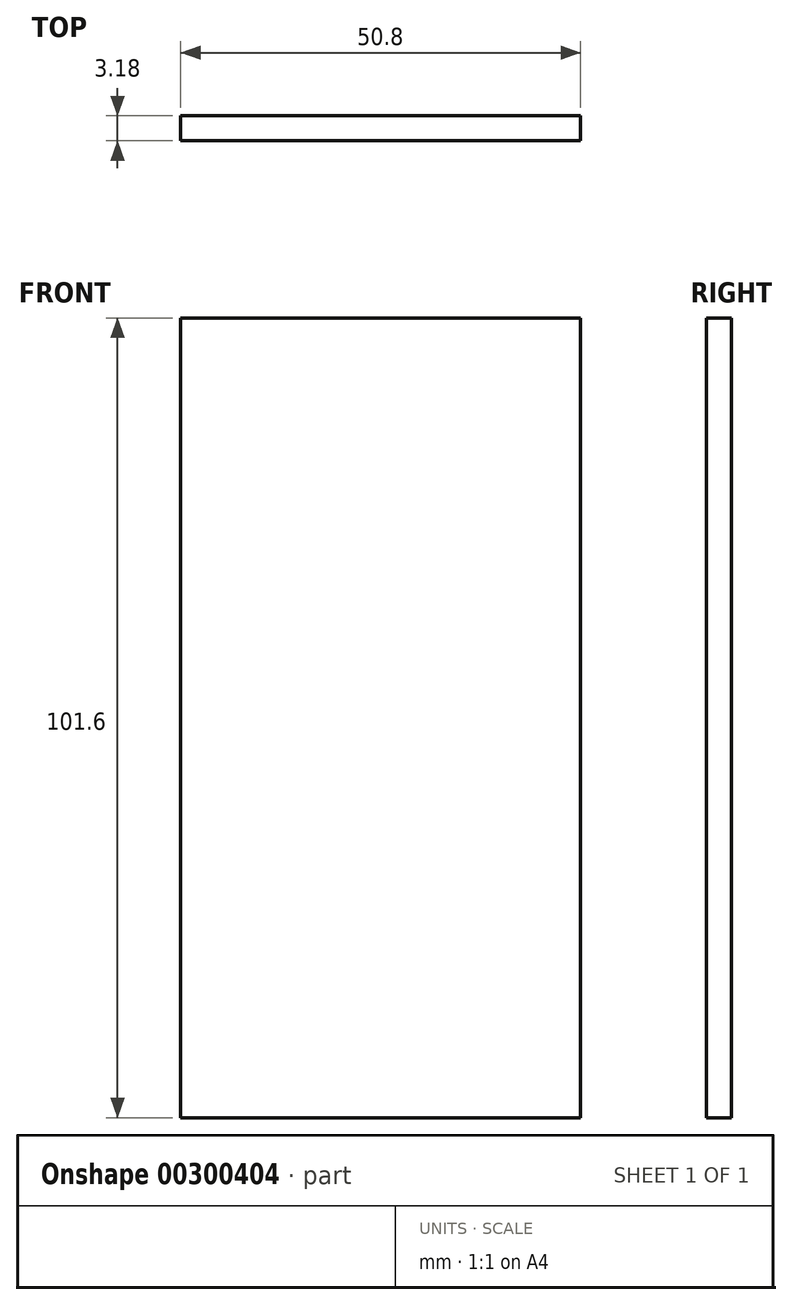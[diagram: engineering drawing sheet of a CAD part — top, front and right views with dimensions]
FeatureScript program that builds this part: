
annotation { "Feature Type Name" : "Feature", "Feature Type Description" : "" }
export const myFeature = defineFeature(function(context is Context, id is Id, definition is map)
    precondition{}
    {
        {
            var Q0;
            Q0=qCreatedBy(makeId("Front.planeOp"),FACE);
            var sketch = newSketch(context, id + "F0", { "sketchPlane" : qUnion([Q0])});
            skLineSegment(sketch, "E0.bottom", {"start": v(25.4, 50.8) * mm, "end": v(-25.4, 50.8) * mm});
            skLineSegment(sketch, "E0.top", {"start": v(25.4, -50.8) * mm, "end": v(-25.4, -50.8) * mm});
            skLineSegment(sketch, "E0.left", {"start": v(25.4, 50.8) * mm, "end": v(25.4, -50.8) * mm});
            skLineSegment(sketch, "E0.right", {"start": v(-25.4, 50.8) * mm, "end": v(-25.4, -50.8) * mm});
            skPoint(sketch, "E0.middle", {"position": v(0, 0) * mm});
            skSolve(sketch);
        }
        {
            var Q0;
            Q0 = qSketchRegion(id + "F0", true);
            extrude(context, id + "F1", {"entities" : qUnion([Q0]), "endBound" : BoundingType.SYMMETRIC, "depth" : 3.17 * mm});
        }
    });
